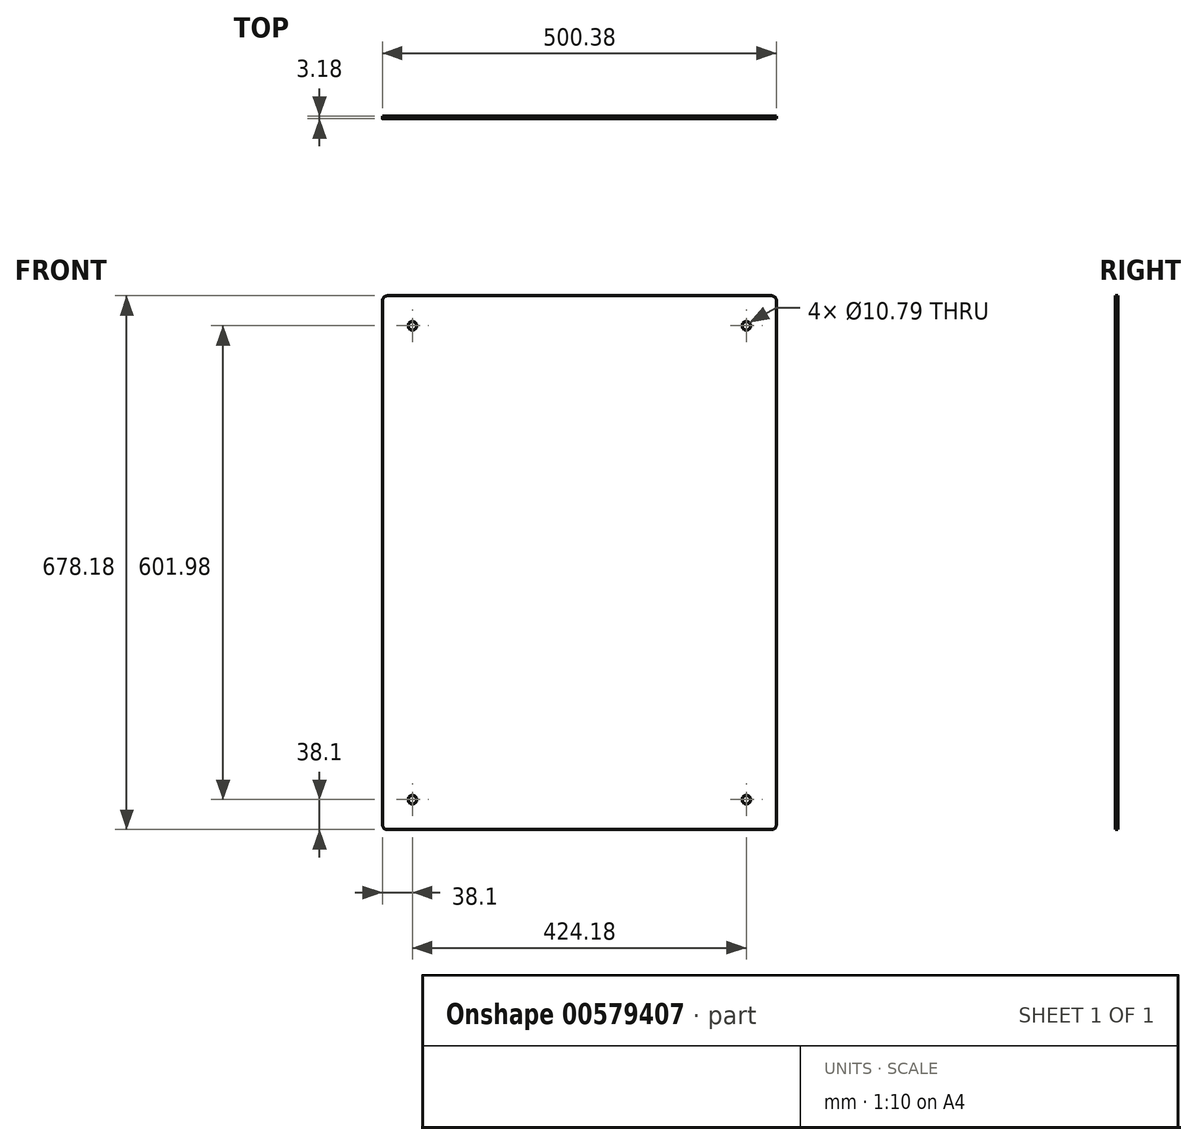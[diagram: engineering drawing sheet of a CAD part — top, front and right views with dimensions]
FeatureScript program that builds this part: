
annotation { "Feature Type Name" : "Feature", "Feature Type Description" : "" }
export const myFeature = defineFeature(function(context is Context, id is Id, definition is map)
    precondition{}
    {
        {
            var Q0;
            Q0=qCreatedBy(makeId("Front.planeOp"),FACE);
            var sketch = newSketch(context, id + "F0", { "sketchPlane" : qUnion([Q0])});
            skLineSegment(sketch, "E0.bottom", {"start": v(243.84, -339.1) * mm, "end": v(-243.84, -339.1) * mm});
            skLineSegment(sketch, "E0.top", {"start": v(243.84, 339.09) * mm, "end": v(-243.84, 339.09) * mm});
            skLineSegment(sketch, "E0.left", {"start": v(250.19, -332.74) * mm, "end": v(250.19, 332.74) * mm});
            skLineSegment(sketch, "E0.right", {"start": v(-250.19, -332.74) * mm, "end": v(-250.19, 332.74) * mm});
            skPoint(sketch, "E0.middle", {"position": v(0, 0) * mm});
            skLineSegment(sketch, "E1.bottom", {"start": v(212.1, -301) * mm, "end": v(-212.1, -301) * mm, "construction": true});
            skLineSegment(sketch, "E1.top", {"start": v(212.09, 301) * mm, "end": v(-212.1, 301) * mm, "construction": true});
            skLineSegment(sketch, "E1.left", {"start": v(212.1, -300.99) * mm, "end": v(212.1, 301) * mm, "construction": true});
            skLineSegment(sketch, "E1.right", {"start": v(-212.1, -300.99) * mm, "end": v(-212.1, 301) * mm, "construction": true});
            skCircle(sketch, "E2", {"center": v(-212.1, 301) * mm, "radius": 5.4 * mm});
            skCircle(sketch, "E3", {"center": v(212.1, 301) * mm, "radius": 5.4 * mm});
            skCircle(sketch, "E4", {"center": v(212.1, -300.99) * mm, "radius": 5.4 * mm});
            skCircle(sketch, "E5", {"center": v(-212.1, -300.99) * mm, "radius": 5.4 * mm});
            skPoint(sketch, "E6.visualSharp", {"position": v(-250.19, 339.09) * mm});
            skArc(sketch, "E6.filletArc", {"start": v(-243.84, 339.1) * mm, "mid": v(-248.33, 337.23) * mm, "end": v(-250.2, 332.74) * mm});
            skPoint(sketch, "E7.visualSharp", {"position": v(250.19, 339.09) * mm});
            skArc(sketch, "E7.filletArc", {"start": v(250.2, 332.74) * mm, "mid": v(248.33, 337.23) * mm, "end": v(243.84, 339.1) * mm});
            skPoint(sketch, "E8.visualSharp", {"position": v(250.19, -339.1) * mm});
            skArc(sketch, "E8.filletArc", {"start": v(243.84, -339.1) * mm, "mid": v(248.33, -337.23) * mm, "end": v(250.2, -332.74) * mm});
            skPoint(sketch, "E9.visualSharp", {"position": v(-250.19, -339.1) * mm});
            skArc(sketch, "E9.filletArc", {"start": v(-250.2, -332.74) * mm, "mid": v(-248.33, -337.23) * mm, "end": v(-243.84, -339.1) * mm});
            skSolve(sketch);
        }
        {
            var Q0;
            Q0=makeQuery(id+"F0.imprint","IMPRINT",FACE,{"disambiguationData":[TD([[makeQuery(id+"F0.imprint","IMPRINT",EDGE,{"derivedFrom":sQuery(id+"F0.wireOp",EDGE,"E0.bottom")}),-1.0]])]});
            extrude(context, id + "F1", {"entities" : qUnion([Q0]), "depth" : 3.17 * mm, "offsetDistance" : 25.4 * mm});
        }
    });
